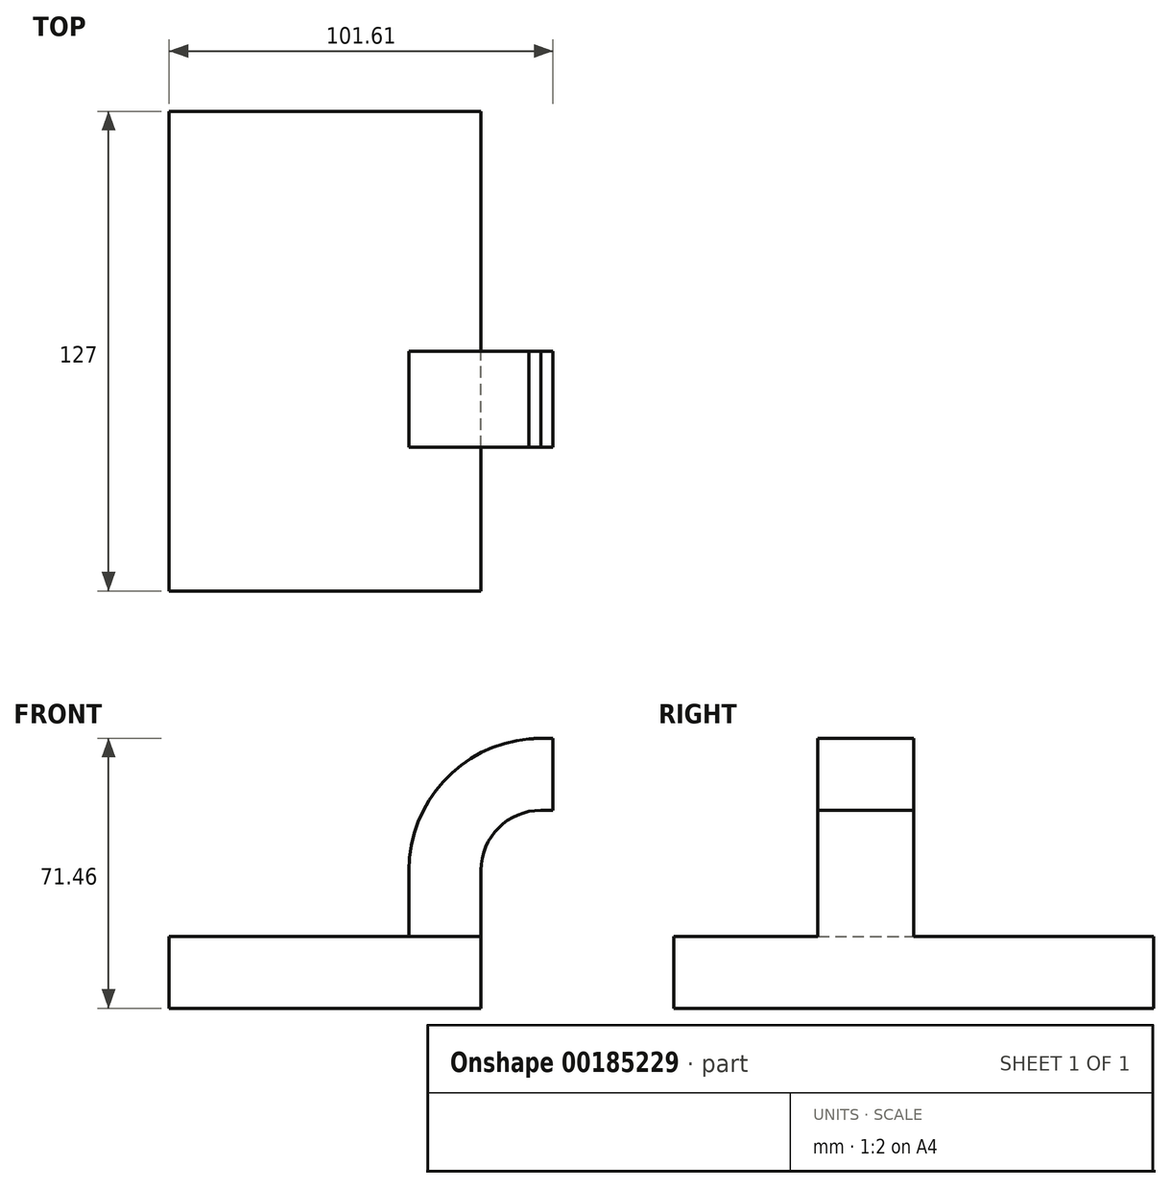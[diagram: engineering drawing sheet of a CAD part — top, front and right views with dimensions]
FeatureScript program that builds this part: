
annotation { "Feature Type Name" : "Feature", "Feature Type Description" : "" }
export const myFeature = defineFeature(function(context is Context, id is Id, definition is map)
    precondition{}
    {
        {
            var Q0;
            Q0=qCreatedBy(makeId("Front.planeOp"),FACE);
            var sketch = newSketch(context, id + "F0", { "sketchPlane" : qUnion([Q0])});
            skLineSegment(sketch, "E0.bottom", {"start": v(41.27, 9.53) * mm, "end": v(-41.28, 9.53) * mm});
            skLineSegment(sketch, "E0.top", {"start": v(41.28, -9.52) * mm, "end": v(-41.27, -9.52) * mm});
            skLineSegment(sketch, "E0.left", {"start": v(41.28, 9.53) * mm, "end": v(41.28, -9.52) * mm});
            skLineSegment(sketch, "E0.right", {"start": v(-41.28, 9.53) * mm, "end": v(-41.27, -9.52) * mm});
            skPoint(sketch, "E0.middle", {"position": v(0, 0) * mm});
            skLineSegment(sketch, "E1.bottom", {"start": v(60.32, 38.1) * mm, "end": v(111.12, 38.1) * mm});
            skLineSegment(sketch, "E1.top", {"start": v(60.32, 66.68) * mm, "end": v(111.12, 66.68) * mm});
            skLineSegment(sketch, "E1.left", {"start": v(60.32, 38.1) * mm, "end": v(60.32, 66.68) * mm});
            skLineSegment(sketch, "E1.right", {"start": v(111.12, 38.1) * mm, "end": v(111.12, 66.68) * mm});
            skPoint(sketch, "E1.middle", {"position": v(85.72, 52.39) * mm});
            skLineSegment(sketch, "E2", {"start": v(41.27, 9.53) * mm, "end": v(41.27, 27) * mm});
            skArc(sketch, "E3", {"start": v(41.27, 27) * mm, "mid": v(45.92, 38.23) * mm, "end": v(57.15, 42.88) * mm});
            skLineSegment(sketch, "E4", {"start": v(57.15, 42.88) * mm, "end": v(85.72, 42.88) * mm});
            skLineSegment(sketch, "E5.0", {"start": v(57.15, 61.93) * mm, "end": v(85.72, 61.93) * mm});
            skArc(sketch, "E5.1", {"start": v(22.23, 27) * mm, "mid": v(32.45, 51.7) * mm, "end": v(57.15, 61.93) * mm});
            skLineSegment(sketch, "E5.2", {"start": v(22.22, 9.53) * mm, "end": v(22.22, 27) * mm});
            skLineSegment(sketch, "E6", {"start": v(85.72, 38.1) * mm, "end": v(85.72, 66.68) * mm});
            skFitSpline(sketch, "E7", {"points": [v(-41.28, 9.52) * mm, v(57.15, 61.93) * mm], "startDerivative": vector(-0.43, 61.8) * mm, "endDerivative": vector(118.66, 3.19) * mm});
            skSolve(sketch);
        }
        {
            var Q0;
            Q0=makeQuery(id+"F0.imprint","IMPRINT",FACE,{"disambiguationData":[TD([[makeQuery(id+"F0.imprint","IMPRINT",EDGE,{"derivedFrom":sQuery(id+"F0.wireOp",EDGE,"E0.top")}),-1.0]])]});
            extrude(context, id + "F1", {"entities" : qUnion([Q0]), "endBound" : BoundingType.SYMMETRIC, "depth" : 127 * mm});
        }
        {
            var Q0;
            {var subQ1=sQuery(id+"F0.wireOp",EDGE,"E2");Q0=makeQuery(id+"F0.imprint","IMPRINT",FACE,{"disambiguationData":[TD([[makeQuery(id+"F0.imprint","IMPRINT",EDGE,{"derivedFrom":subQ1}),1.0]])]});}
            extrude(context, id + "F2", {"entities" : qUnion([Q0]), "operationType" : NewBodyOperationType.ADD, "depth" : 25.4 * mm});
        }
    });
